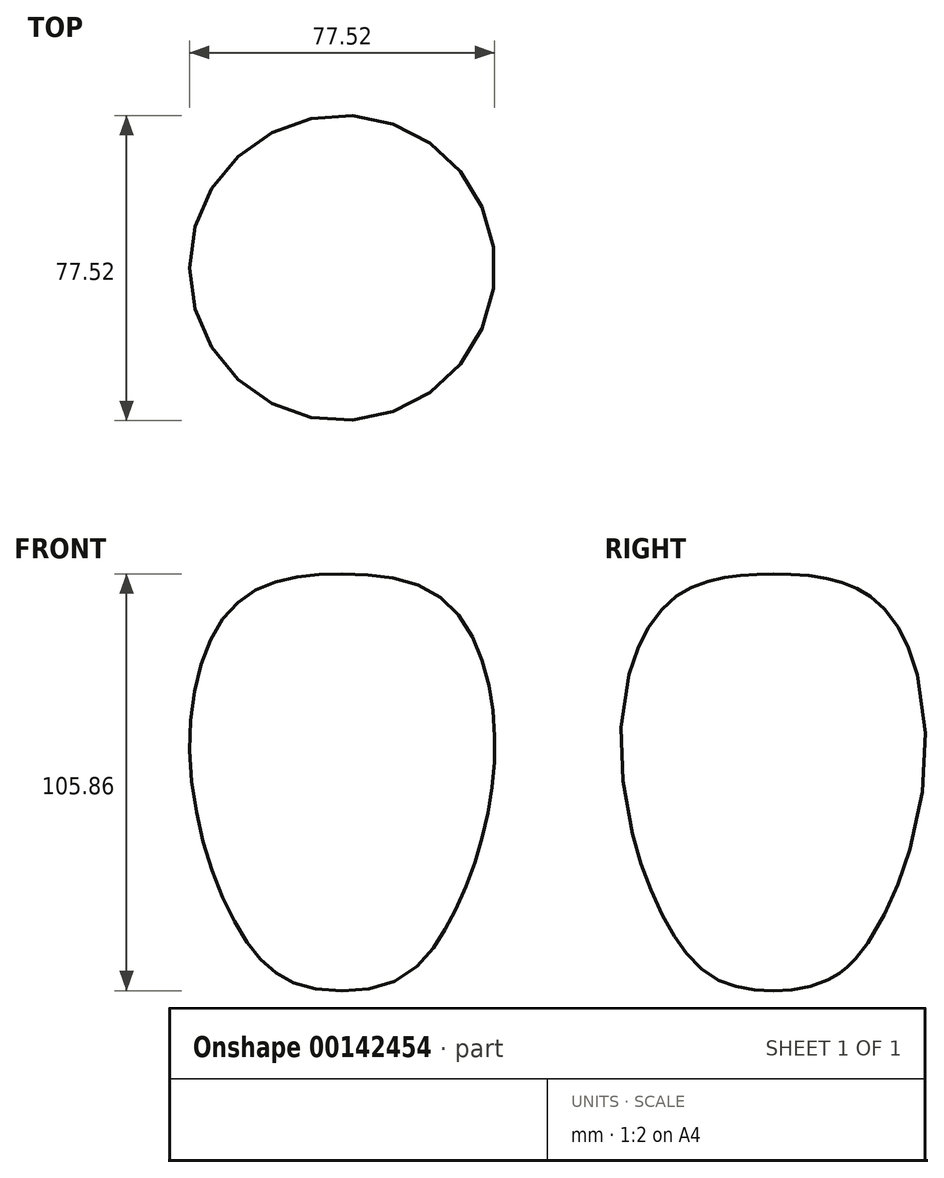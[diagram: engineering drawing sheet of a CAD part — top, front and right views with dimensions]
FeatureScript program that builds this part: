
annotation { "Feature Type Name" : "Feature", "Feature Type Description" : "" }
export const myFeature = defineFeature(function(context is Context, id is Id, definition is map)
    precondition{}
    {
        {
            var Q0;
            Q0=qCreatedBy(makeId("Front.planeOp"),FACE);
            var sketch = newSketch(context, id + "F0", { "sketchPlane" : qUnion([Q0])});
            skFitSpline(sketch, "E0", {"points": [v(0, 50.19) * mm, v(-26.85, 42.7) * mm, v(-38.69, 3.32) * mm, v(-24.2, -43.28) * mm, v(0, -55.67) * mm], "startDerivative": vector(-134.28, 0) * mm, "endDerivative": vector(172.72, 0) * mm});
            skFitSpline(sketch, "E1.MirrorCS", {"points": [v(0, 50.19) * mm, v(26.85, 42.7) * mm, v(38.69, 3.32) * mm, v(24.2, -43.28) * mm, v(0, -55.67) * mm], "startDerivative": vector(134.28, 0) * mm, "endDerivative": vector(-172.72, 0) * mm});
            skLineSegment(sketch, "E2", {"start": v(0, 50.19) * mm, "end": v(0, -55.67) * mm});
            skSolve(sketch);
        }
        {
            var Q0;
            Q0=makeQuery(id+"F0.imprint","IMPRINT",FACE,{"disambiguationData":[TD([[makeQuery(id+"F0.imprint","IMPRINT",EDGE,{"derivedFrom":sQuery(id+"F0.wireOp",EDGE,"E0")}),1.0]])]});
            var Q1;
            Q1=sQuery(id+"F0.wireOp",EDGE,"E2");
            revolve(context, id + "F1", {"entities" : qUnion([Q0]), "axis" : qUnion([Q1]), "revolveType" : RevolveType.FULL});
        }
    });
